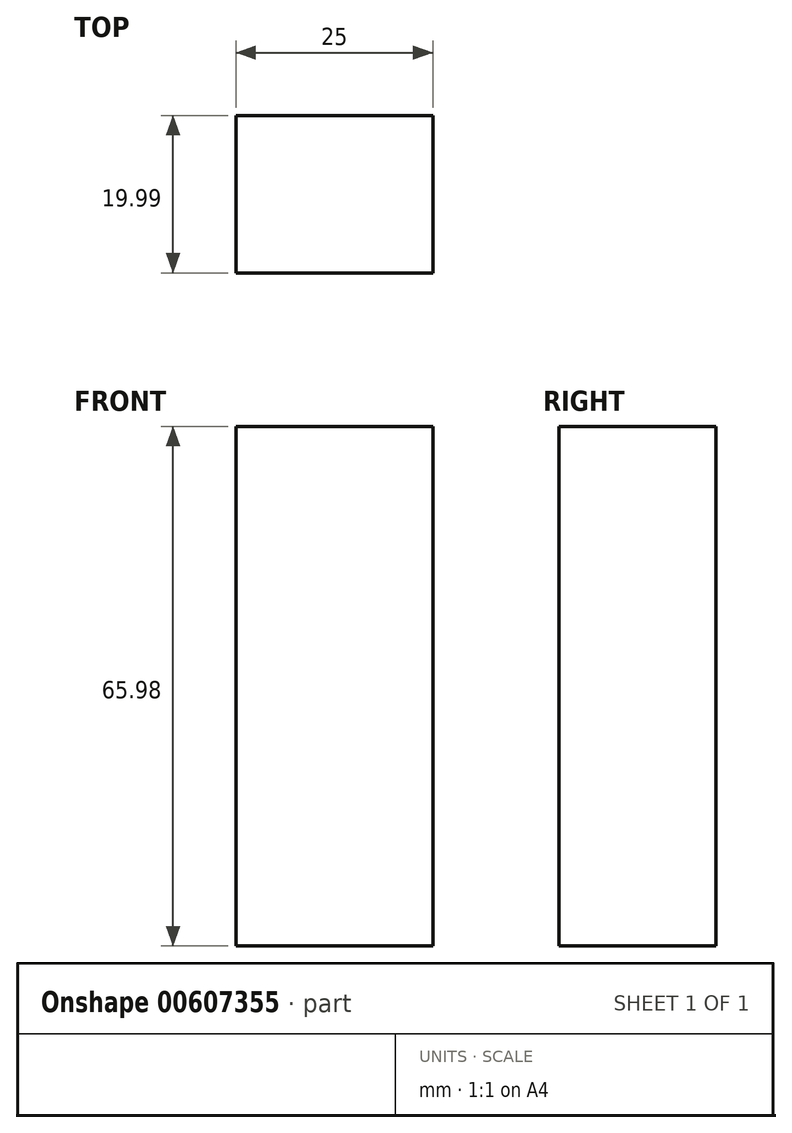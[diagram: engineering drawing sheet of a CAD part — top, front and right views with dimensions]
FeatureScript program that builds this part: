
annotation { "Feature Type Name" : "Feature", "Feature Type Description" : "" }
export const myFeature = defineFeature(function(context is Context, id is Id, definition is map)
    precondition{}
    {
        {
            var Q0;
            Q0=qCreatedBy(makeId("Front.planeOp"),FACE);
            var sketch = newSketch(context, id + "F0", { "sketchPlane" : qUnion([Q0])});
            skLineSegment(sketch, "E0.bottom", {"start": v(12.5, -33) * mm, "end": v(-12.5, -33) * mm});
            skLineSegment(sketch, "E0.top", {"start": v(12.5, 33) * mm, "end": v(-12.5, 33) * mm});
            skLineSegment(sketch, "E0.left", {"start": v(12.5, -33) * mm, "end": v(12.5, 33) * mm});
            skLineSegment(sketch, "E0.right", {"start": v(-12.5, -33) * mm, "end": v(-12.5, 33) * mm});
            skPoint(sketch, "E0.middle", {"position": v(0, 0) * mm});
            skSolve(sketch);
        }
        {
            var Q0;
            Q0 = qSketchRegion(id + "F0", true);
            extrude(context, id + "F1", {"entities" : qUnion([Q0]), "depth" : 19.99 * mm, "offsetDistance" : 25.4 * mm});
        }
    });
